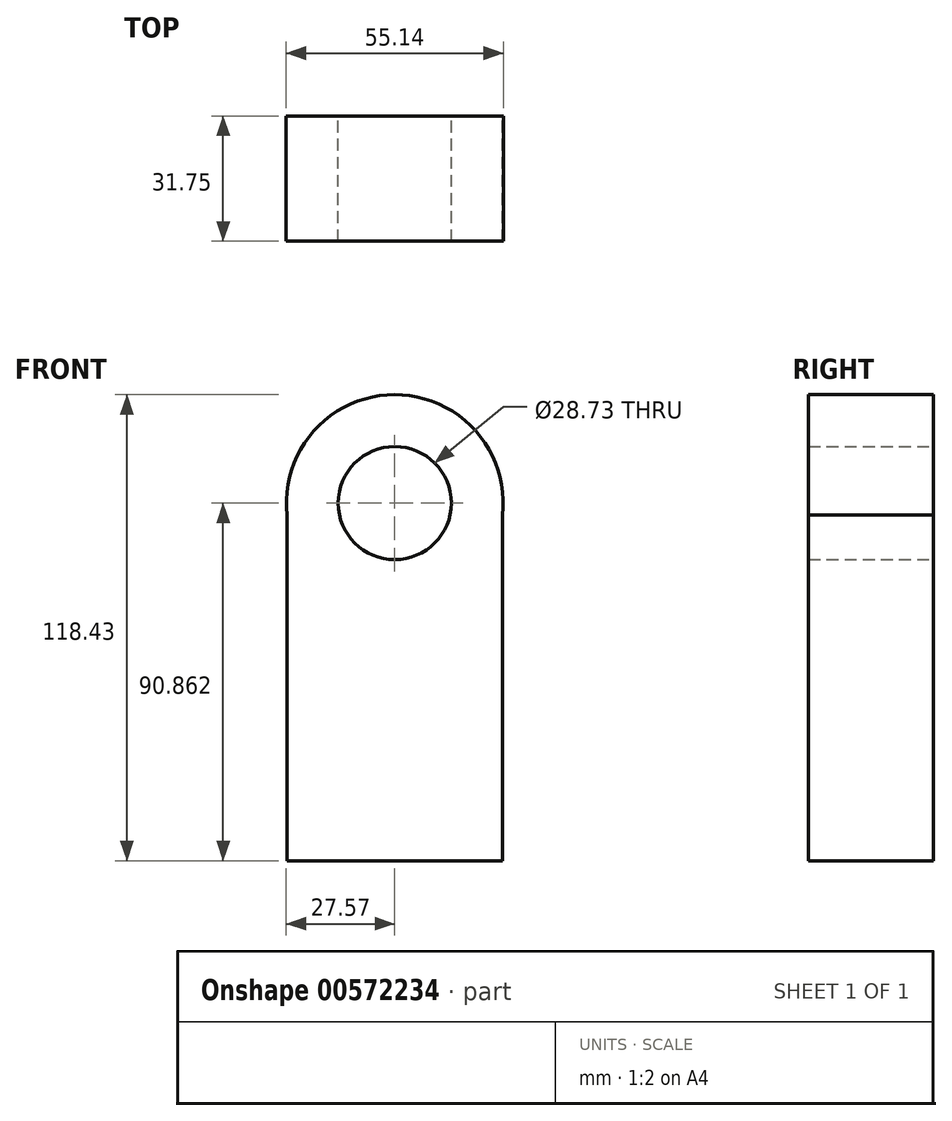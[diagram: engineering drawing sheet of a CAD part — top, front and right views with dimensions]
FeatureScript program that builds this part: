
annotation { "Feature Type Name" : "Feature", "Feature Type Description" : "" }
export const myFeature = defineFeature(function(context is Context, id is Id, definition is map)
    precondition{}
    {
        {
            var Q0;
            Q0=qCreatedBy(makeId("Front.planeOp"),FACE);
            var sketch = newSketch(context, id + "F0", { "sketchPlane" : qUnion([Q0])});
            skLineSegment(sketch, "E0.top", {"start": v(27.4, -45.43) * mm, "end": v(-27.4, -45.43) * mm});
            skLineSegment(sketch, "E0.left", {"start": v(27.4, 45.43) * mm, "end": v(27.4, -45.43) * mm});
            skLineSegment(sketch, "E0.right", {"start": v(-27.4, 45.43) * mm, "end": v(-27.4, -45.43) * mm});
            skPoint(sketch, "E0.middle", {"position": v(0, 0) * mm});
            skArc(sketch, "E1", {"start": v(27.4, 42.36) * mm, "mid": v(0, 73) * mm, "end": v(-27.4, 42.36) * mm});
            skCircle(sketch, "E2", {"center": v(0, 45.43) * mm, "radius": 14.37 * mm});
            skSolve(sketch);
        }
        {
            var Q0;
            {var subQ2=sQuery(id+"F0.wireOp",EDGE,"E0.top");Q0=makeQuery(id+"F0.imprint","IMPRINT",FACE,{"disambiguationData":[TD([[makeQuery(id+"F0.imprint","IMPRINT",EDGE,{"derivedFrom":subQ2}),-1.0]])]});}
            extrude(context, id + "F1", {"entities" : qUnion([Q0]), "depth" : 31.75 * mm, "offsetDistance" : 25.4 * mm});
        }
    });
